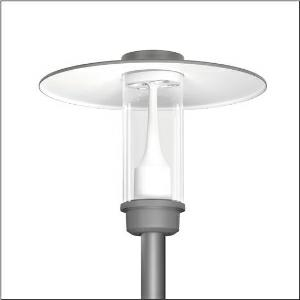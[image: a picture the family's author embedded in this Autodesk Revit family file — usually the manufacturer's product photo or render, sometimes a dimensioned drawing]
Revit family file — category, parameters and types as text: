
# Revit family: litepole_2_iq___st1_2a_5xa5425af14h_a18f
name_source: partatom
category: Lighting Fixtures
units: mm (PartAtom-declared; Revit-internal decimal feet)

## family parameters
Cut with Voids When Loaded = No
Host = Face
Light Source = No
Part Type = Normal
Room Calculation Point = No
Round Connector Dimension = Use Diameter
Shared = No

## types (1)
- --- (1 x LED, 1550 lm, 12.9 W, 2200K)
    Apparent Load = 13 VA
    CIE Flux Codes = 22 60 92 98 100
    Color Rendering = 70
    Color Temperature = 2200K
    Default Elevation = 1800 mm
    Description = Litepole 2 iQ, mast luminaire, Module 540 iQ-SR, primary light control with 3 zone facetted reflector, of plastic, silver coated, highly specular, structured, primary optical cover: cover, of PMMA, transparent, light distribution: ST1.2a, light emission: direct distribution, primary light characteristic: asymmetric, installation type: post-top, LED, High Power LED, rated luminous flux: 1.550lm, luminous efficacy: 120lm/W, light colour: 722, colour temperature: 2200K, control gear: iQ Street-Remote, control: pre-setting: logarithmic dimming characteristic, Street-Remote, Auto-Match, Temp-Guard, Lumen-Switch, Night-Set, Smart-Wire, Light-Fading, Desk-Remote (wireless, voltage-free reading and setting of iQ features in the workshop via application-optimized NFC function/RFID function), optimised constant luminous flux control (CLO 2.0), with terminal, 6-pole, max. 2.5mm², mains connection: 230..240V, AC, 50/60Hz, start of lifetime: 13W, end of service life: 13W, reduction: 6W, luminaire housing, upper part, of aluminium, coated, Siteco® metallic grey (DB 702S), diameter: 750mm, height: 590mm, spigot size: d x l = 76 x 70mm (post-top) | with reducer (optional accessory) 60 x 70mm, mounting height: 3..5m, post-top mast mounting element, of diecast aluminium, coated, Siteco® metallic grey (DB 702S), Module 540 iQ-SR, traffic white (RAL 9016), equipment: standard, protection rating (complete): IP65, insulation class (complete): insulation class II (safety insulation), certification: CE, ENEC, VDE, packaging unit: 1 piece

Light Distribution: ST1.2a
    Height = 590 mm
    Lamp = 1 x LED
    Lamp Light Flux = 1550 lm
    Lamp Power = 12.9 W
    Lamp count = 1
    Length = 750 mm
    Luminous efficacy = 120 lm/W
    Manufacturer = Siteco
    ModVariant = No
    Model = 5XA5425AF14H
    Number of Poles = 1
    OnlyDefault = Yes
    Power Factor = 1
    Product Name = Litepole 2 iQ | ST1.2a
    Product group = mast luminaire | pylon top
    ProductGroupID = 6100
    Protection Class = Protection class II
    Protection Degree = IP 65
    RLX_Detail_Level = 1
    RLX_Emergency_Light_Flux = 0 lm
    RLX_Emergency_Type = 0
    RLX_Emergency_Type_DB = No
    RlxData = <blob elided: 64201 chars, md5=45b5fbba>
    Socket = socket
    Standby Power = 0 W
    System Light Flux = 1550 lm
    System Power = 13 W
    Type Comments = factory setting: luminous flux: 100 % | dim-lin: 254 | 516 mA
    Type Image = l_1006518.jpg
    URL = http://relux.com
    VarID = @adj_190139
    Voltage = 0 V
    Weight = 0.00 kg
    Width = 0 mm  [stored 0 ft]

note: [stored X ft] marks values corroborated as IEEE doubles in the binary element streams (Revit-internal decimal feet)

## geometry (parser evidence)
native form markers: Blend x4, Sweep x11
no freeform markers — native parametric forms only
